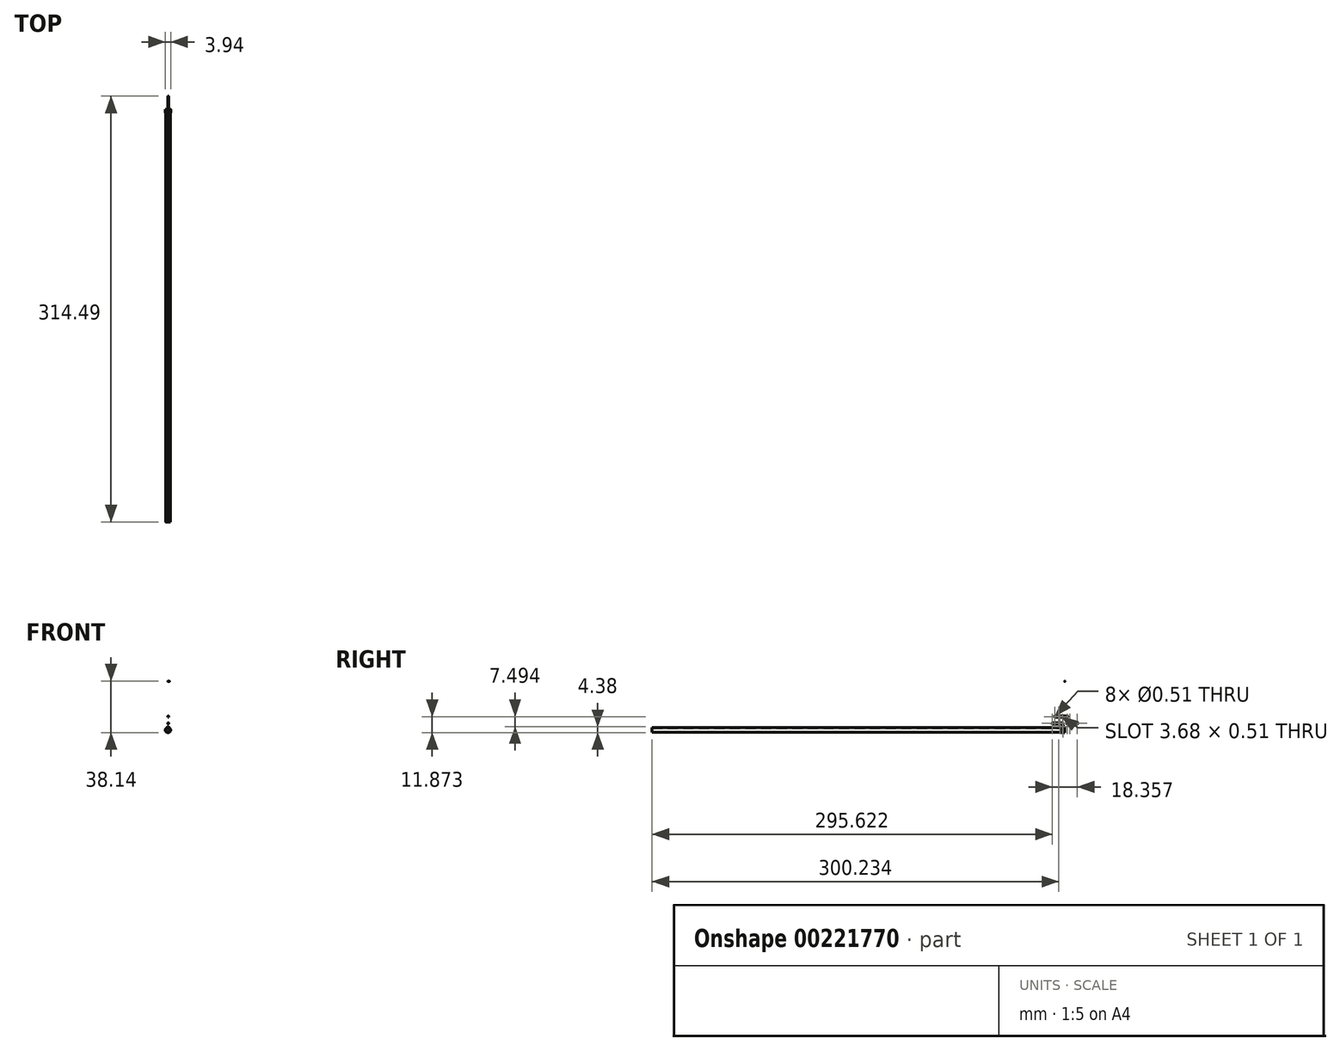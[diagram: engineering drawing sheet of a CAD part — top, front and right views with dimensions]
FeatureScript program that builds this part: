
annotation { "Feature Type Name" : "Feature", "Feature Type Description" : "" }
export const myFeature = defineFeature(function(context is Context, id is Id, definition is map)
    precondition{}
    {
        {
            var Q0;
            Q0=qCreatedBy(makeId("Right.planeOp"),FACE);
            var sketch = newSketch(context, id + "F0", { "sketchPlane" : qUnion([Q0])});
            skLineSegment(sketch, "E0.bottom", {"start": v(-9.69, 5.4) * mm, "end": v(-1.17, 5.4) * mm});
            skLineSegment(sketch, "E0.top", {"start": v(-9.69, 4.38) * mm, "end": v(-1.17, 4.38) * mm});
            skLineSegment(sketch, "E0.left", {"start": v(-9.69, 5.4) * mm, "end": v(-9.69, 4.38) * mm});
            skLineSegment(sketch, "E0.right", {"start": v(-1.17, 5.4) * mm, "end": v(-1.17, 4.38) * mm});
            skCircle(sketch, "E1", {"center": v(-9.18, 4.9) * mm, "radius": 0.25 * mm});
            skCircle(sketch, "E2", {"center": v(-1.68, 4.9) * mm, "radius": 0.25 * mm});
            skCircle(sketch, "E3", {"center": v(-3.71, 4.9) * mm, "radius": 0.25 * mm});
            skLineSegment(sketch, "E4", {"start": v(-9.69, 4.9) * mm, "end": v(-1.17, 4.9) * mm, "construction": true});
            skLineSegment(sketch, "E5.MirrorCS", {"start": v(-9.69, 4.38) * mm, "end": v(-9.69, 5.4) * mm});
            skLineSegment(sketch, "E6.MirrorCS", {"start": v(-1.17, 4.38) * mm, "end": v(-1.17, 5.4) * mm});
            skLineSegment(sketch, "E7", {"start": v(0, 0) * mm, "end": v(0, 11.35) * mm, "construction": true});
            skLineSegment(sketch, "E8.MirrorCS", {"start": v(9.69, 5.4) * mm, "end": v(9.69, 4.38) * mm});
            skLineSegment(sketch, "E9.MirrorCS", {"start": v(1.17, 4.38) * mm, "end": v(1.17, 5.4) * mm});
            skCircle(sketch, "E10.MirrorC", {"center": v(1.68, 4.9) * mm, "radius": 0.25 * mm});
            skCircle(sketch, "E11.MirrorC", {"center": v(3.71, 4.9) * mm, "radius": 0.25 * mm});
            skLineSegment(sketch, "E12.MirrorCS", {"start": v(9.69, 5.4) * mm, "end": v(1.17, 5.4) * mm});
            skLineSegment(sketch, "E13.MirrorCS", {"start": v(9.69, 4.38) * mm, "end": v(1.17, 4.38) * mm});
            skCircle(sketch, "E14.MirrorC", {"center": v(9.18, 4.9) * mm, "radius": 0.25 * mm});
            skLineSegment(sketch, "E15.MirrorCS", {"start": v(1.17, 5.4) * mm, "end": v(1.17, 4.38) * mm});
            skLineSegment(sketch, "E16.MirrorCS", {"start": v(9.69, 4.38) * mm, "end": v(9.69, 5.4) * mm});
            skLineSegment(sketch, "E17.MirrorCS", {"start": v(9.69, 4.9) * mm, "end": v(1.17, 4.9) * mm, "construction": true});
            skLineSegment(sketch, "E18.bottom", {"start": v(-7.93, 10.41) * mm, "end": v(2.36, 10.41) * mm});
            skLineSegment(sketch, "E18.top", {"start": v(-7.93, 9.4) * mm, "end": v(2.36, 9.4) * mm});
            skLineSegment(sketch, "E18.left", {"start": v(-7.93, 10.41) * mm, "end": v(-7.93, 9.4) * mm});
            skLineSegment(sketch, "E18.right", {"start": v(2.36, 10.41) * mm, "end": v(2.36, 9.4) * mm});
            skLineSegment(sketch, "E19", {"start": v(-7.93, 9.9) * mm, "end": v(2.36, 9.9) * mm, "construction": true});
            skCircle(sketch, "E20", {"center": v(-7.42, 9.9) * mm, "radius": 0.25 * mm});
            skLineSegment(sketch, "E21.bottom", {"start": v(-6.15, 10.16) * mm, "end": v(-2.98, 10.16) * mm});
            skLineSegment(sketch, "E21.top", {"start": v(-6.15, 9.65) * mm, "end": v(-2.98, 9.65) * mm});
            skLineSegment(sketch, "E21.left", {"start": v(-6.4, 9.9) * mm, "end": v(-6.4, 9.9) * mm});
            skLineSegment(sketch, "E21.right", {"start": v(-2.72, 9.9) * mm, "end": v(-2.72, 9.9) * mm});
            skPoint(sketch, "E22", {"position": v(-6.4, 9.9) * mm});
            skPoint(sketch, "E23.visualSharp", {"position": v(-2.72, 10.16) * mm});
            skArc(sketch, "E23.filletArc", {"start": v(-2.72, 9.9) * mm, "mid": v(-2.8, 10.08) * mm, "end": v(-2.98, 10.16) * mm});
            skPoint(sketch, "E24.visualSharp", {"position": v(-2.72, 9.65) * mm});
            skArc(sketch, "E24.filletArc", {"start": v(-2.98, 9.65) * mm, "mid": v(-2.8, 9.72) * mm, "end": v(-2.72, 9.9) * mm});
            skPoint(sketch, "E25.visualSharp", {"position": v(-6.4, 10.16) * mm});
            skArc(sketch, "E25.filletArc", {"start": v(-6.15, 10.16) * mm, "mid": v(-6.33, 10.08) * mm, "end": v(-6.4, 9.9) * mm});
            skPoint(sketch, "E26.visualSharp", {"position": v(-6.4, 9.65) * mm});
            skArc(sketch, "E26.filletArc", {"start": v(-6.4, 9.9) * mm, "mid": v(-6.33, 9.72) * mm, "end": v(-6.15, 9.65) * mm});
            skSolve(sketch);
        }
        {
            var Q0;
            Q0 = qSketchRegion(id + "F0", true);
            extrude(context, id + "F1", {"entities" : qUnion([Q0]), "depth" : 0.5 * mm});
        }
        {
            var Q0;
            Q0=makeQuery(id+"F1.opExtrude","SWEPT_EDGE",EDGE,{"disambiguationData":[OSD([sQuery(id+"F0.wireOp",EDGE,"E18.bottom"),sQuery(id+"F0.wireOp",EDGE,"E18.left")])]});
            var Q1;
            Q1=makeQuery(id+"F1.opExtrude","SWEPT_EDGE",EDGE,{"disambiguationData":[OSD([sQuery(id+"F0.wireOp",EDGE,"E18.top"),sQuery(id+"F0.wireOp",EDGE,"E18.left")])]});
            var Q2;
            Q2=makeQuery(id+"F1.opExtrude","SWEPT_EDGE",EDGE,{"disambiguationData":[OSD([sQuery(id+"F0.wireOp",EDGE,"E18.bottom"),sQuery(id+"F0.wireOp",EDGE,"E18.right")])]});
            var Q3;
            Q3=makeQuery(id+"F1.opExtrude","SWEPT_EDGE",EDGE,{"disambiguationData":[OSD([sQuery(id+"F0.wireOp",EDGE,"E18.top"),sQuery(id+"F0.wireOp",EDGE,"E18.right")])]});
            var Q4;
            Q4=makeQuery(id+"F1.opExtrude","SWEPT_EDGE",EDGE,{"disambiguationData":[OSD([sQuery(id+"F0.wireOp",EDGE,"E16.MirrorCS"),sQuery(id+"F0.wireOp",EDGE,"E12.MirrorCS")])]});
            var Q5;
            Q5=makeQuery(id+"F1.opExtrude","SWEPT_EDGE",EDGE,{"disambiguationData":[OSD([sQuery(id+"F0.wireOp",EDGE,"E16.MirrorCS"),sQuery(id+"F0.wireOp",EDGE,"E13.MirrorCS")])]});
            var Q6;
            Q6=makeQuery(id+"F1.opExtrude","SWEPT_EDGE",EDGE,{"disambiguationData":[OSD([sQuery(id+"F0.wireOp",EDGE,"E0.bottom"),sQuery(id+"F0.wireOp",EDGE,"E0.right")])]});
            var Q7;
            Q7=makeQuery(id+"F1.opExtrude","SWEPT_EDGE",EDGE,{"disambiguationData":[OSD([sQuery(id+"F0.wireOp",EDGE,"E0.top"),sQuery(id+"F0.wireOp",EDGE,"E0.right")])]});
            var Q8;
            Q8=makeQuery(id+"F1.opExtrude","SWEPT_EDGE",EDGE,{"disambiguationData":[OSD([sQuery(id+"F0.wireOp",EDGE,"E12.MirrorCS"),sQuery(id+"F0.wireOp",EDGE,"E15.MirrorCS")])]});
            var Q9;
            Q9=makeQuery(id+"F1.opExtrude","SWEPT_EDGE",EDGE,{"disambiguationData":[OSD([sQuery(id+"F0.wireOp",EDGE,"E15.MirrorCS"),sQuery(id+"F0.wireOp",EDGE,"E13.MirrorCS")])]});
            var Q10;
            Q10=makeQuery(id+"F1.opExtrude","SWEPT_EDGE",EDGE,{"disambiguationData":[OSD([sQuery(id+"F0.wireOp",EDGE,"E0.bottom"),sQuery(id+"F0.wireOp",EDGE,"E0.left")])]});
            var Q11;
            Q11=makeQuery(id+"F1.opExtrude","SWEPT_EDGE",EDGE,{"disambiguationData":[OSD([sQuery(id+"F0.wireOp",EDGE,"E0.top"),sQuery(id+"F0.wireOp",EDGE,"E0.left")])]});
            fillet(context, id + "F2", {"entities" : qUnion([Q0, Q1, Q2, Q3, Q4, Q5, Q6, Q7, Q8, Q9, Q10, Q11]), "radius" : 0.5 * mm, "tangentPropagation" : true, "allowEdgeOverflow" : false});
        }
        {
            var Q0;
            Q0=qCreatedBy(makeId("Front.planeOp"),FACE);
            var sketch = newSketch(context, id + "F3", { "sketchPlane" : qUnion([Q0])});
            skArc(sketch, "E27", {"start": v(-0.25, 1.7) * mm, "mid": v(0, -1.71) * mm, "end": v(0.25, 1.7) * mm});
            skArc(sketch, "E28", {"start": v(-0.25, 1.24) * mm, "mid": v(0, -1.27) * mm, "end": v(0.25, 1.24) * mm});
            skLineSegment(sketch, "E29", {"start": v(-0.25, 1.7) * mm, "end": v(-0.25, 1.24) * mm});
            skLineSegment(sketch, "E30", {"start": v(0, 0) * mm, "end": v(0, 2.64) * mm, "construction": true});
            skLineSegment(sketch, "E31.MirrorCS", {"start": v(0.25, 1.7) * mm, "end": v(0.25, 1.24) * mm});
            skSolve(sketch);
        }
        {
            var Q0;
            Q0 = qSketchRegion(id + "F3", true);
            extrude(context, id + "F4", {"entities" : qUnion([Q0]), "depth" : 304.8 * mm});
        }
        {
            var Q0;
            Q0=qCreatedBy(makeId("Front.planeOp"),FACE);
            var sketch = newSketch(context, id + "F5", { "sketchPlane" : qUnion([Q0])});
            skArc(sketch, "E32", {"start": v(-0.2, 1.77) * mm, "mid": v(0, -1.78) * mm, "end": v(0.2, 1.77) * mm});
            skArc(sketch, "E33", {"start": v(-0.5, 1.9) * mm, "mid": v(0, -1.97) * mm, "end": v(0.5, 1.9) * mm});
            skLineSegment(sketch, "E34", {"start": v(0, 0) * mm, "end": v(0, 3.84) * mm, "construction": true});
            skLineSegment(sketch, "E35", {"start": v(-0.5, 1.9) * mm, "end": v(-0.5, 2.92) * mm});
            skLineSegment(sketch, "E36", {"start": v(-0.5, 2.92) * mm, "end": v(0, 2.92) * mm});
            skLineSegment(sketch, "E37.MirrorCS", {"start": v(0.5, 1.9) * mm, "end": v(0.5, 2.92) * mm});
            skLineSegment(sketch, "E38.MirrorCS", {"start": v(0.5, 2.92) * mm, "end": v(0, 2.92) * mm});
            skLineSegment(sketch, "E39", {"start": v(-0.2, 1.77) * mm, "end": v(-0.2, 1.27) * mm});
            skLineSegment(sketch, "E40", {"start": v(-0.2, 1.27) * mm, "end": v(0.2, 1.27) * mm});
            skLineSegment(sketch, "E41", {"start": v(0.2, 1.27) * mm, "end": v(0.2, 1.77) * mm});
            skSolve(sketch);
        }
        {
            var Q0;
            Q0 = qSketchRegion(id + "F5", true);
            extrude(context, id + "F6", {"entities" : qUnion([Q0]), "depth" : 2.54 * mm});
        }
        {
            var Q0;
            Q0=qCreatedBy(makeId("Right.planeOp"),FACE);
            var sketch = newSketch(context, id + "F7", { "sketchPlane" : qUnion([Q0])});
            skCircle(sketch, "E42", {"center": v(-1.27, 2.4) * mm, "radius": 0.25 * mm});
            skSolve(sketch);
        }
        {
            var Q0;
            Q0 = qSketchRegion(id + "F7", true);
            extrude(context, id + "F8", {"entities" : qUnion([Q0]), "operationType" : NewBodyOperationType.REMOVE, "endBound" : BoundingType.THROUGH_ALL, "oppositeDirection" : true, "depth" : 25.4 * mm, "hasSecondDirection" : true, "secondDirectionBound" : SecondDirectionBoundingType.THROUGH_ALL, "secondDirectionOppositeDirection" : false, "secondDirectionDepth" : 25.4 * mm});
        }
        {
            var Q0;
            Q0=qCreatedBy(makeId("Right.planeOp"),FACE);
            var sketch = newSketch(context, id + "F9", { "sketchPlane" : qUnion([Q0])});
            skCircle(sketch, "E43", {"center": v(0, 35.94) * mm, "radius": 0.23 * mm});
            skSolve(sketch);
        }
        {
            var Q0;
            Q0 = qSketchRegion(id + "F9", true);
            extrude(context, id + "F10", {"entities" : qUnion([Q0]), "depth" : 1.02 * mm});
        }
    });
